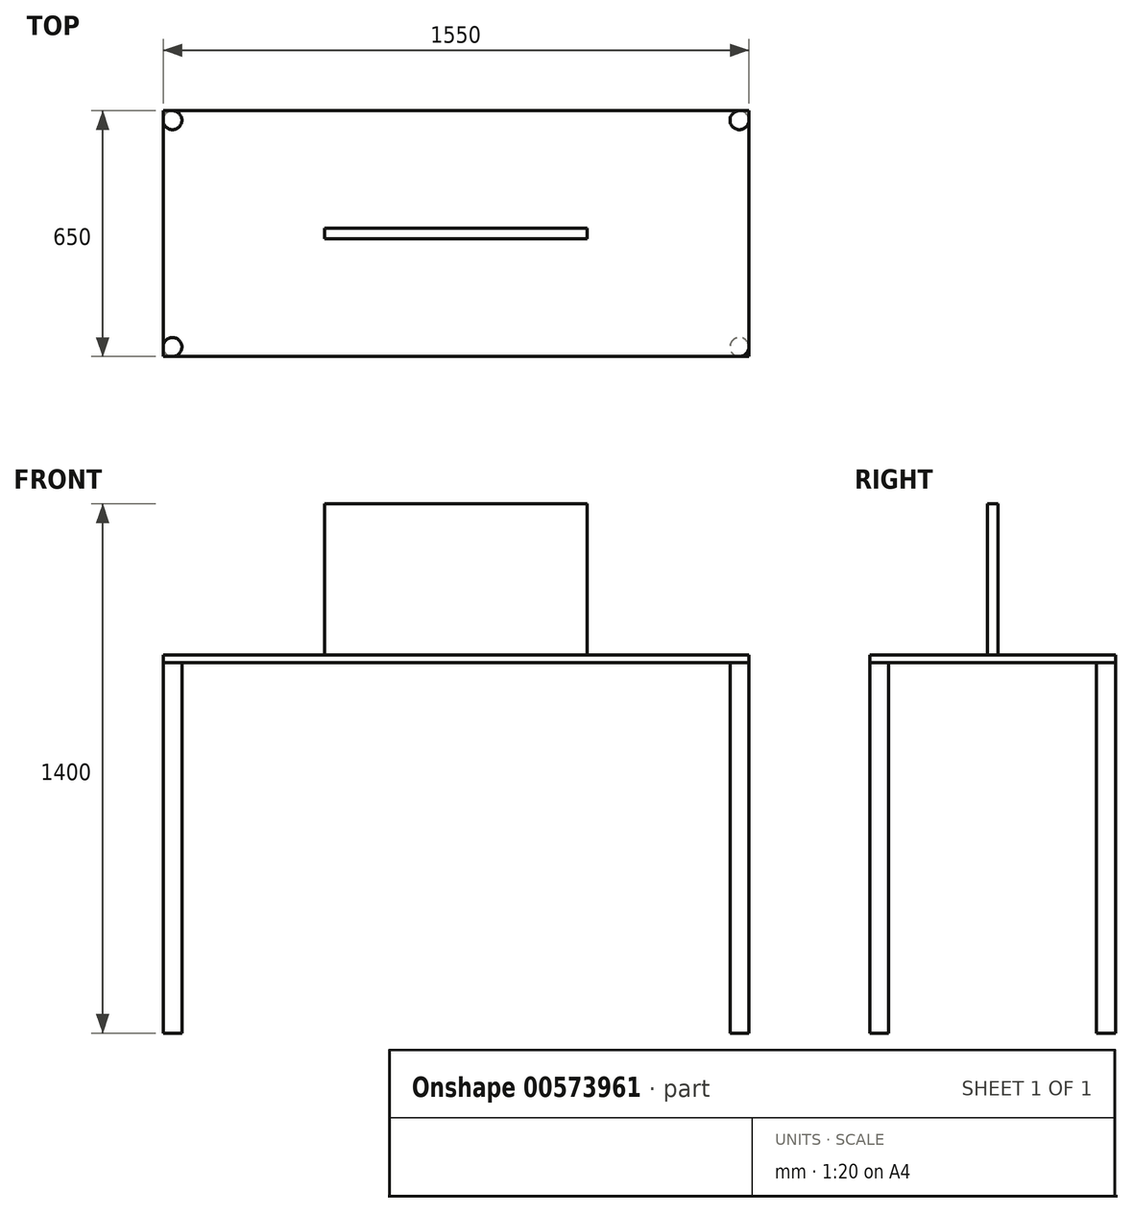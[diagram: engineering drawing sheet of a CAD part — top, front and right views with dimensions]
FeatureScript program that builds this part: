
annotation { "Feature Type Name" : "Feature", "Feature Type Description" : "" }
export const myFeature = defineFeature(function(context is Context, id is Id, definition is map)
    precondition{}
    {
        {
            var Q0;
            Q0=qCreatedBy(makeId("Top.planeOp"),FACE);
            cPlane(context, id + "F0", {"entities" : qUnion([Q0]), "cplaneType" : CPlaneType.OFFSET, "offset" : 1000 * mm, "width" : 150 * mm, "height" : 150 * mm});
        }
        {
            var Q0;
            Q0=qCreatedBy(makeId("Top.planeOp"),FACE);
            var sketch = newSketch(context, id + "F1", { "sketchPlane" : qUnion([Q0])});
            skPoint(sketch, "E0.middle", {"position": v(0, 0) * mm});
            skCircle(sketch, "E1", {"center": v(-750, 300) * mm, "radius": 25 * mm});
            skCircle(sketch, "E2", {"center": v(-750, -300) * mm, "radius": 25 * mm});
            skCircle(sketch, "E3", {"center": v(750, -300) * mm, "radius": 25 * mm});
            skCircle(sketch, "E4", {"center": v(750, 300) * mm, "radius": 25 * mm});
            skSolve(sketch);
        }
        {
            var Q0;
            Q0=qCreatedBy(id+"F0.planeOp",FACE);
            var sketch = newSketch(context, id + "F2", { "sketchPlane" : qUnion([Q0])});
            skLineSegment(sketch, "E5.bottom", {"start": v(775, 325) * mm, "end": v(-775, 325) * mm});
            skLineSegment(sketch, "E5.top", {"start": v(775, -325) * mm, "end": v(-775, -325) * mm});
            skLineSegment(sketch, "E5.left", {"start": v(775, 325) * mm, "end": v(775, -325) * mm});
            skLineSegment(sketch, "E5.right", {"start": v(-775, 325) * mm, "end": v(-775, -325) * mm});
            skSolve(sketch);
        }
        {
            var Q0;
            Q0 = qSketchRegion(id + "F1", true);
            extrude(context, id + "F3", {"entities" : qUnion([Q0]), "depth" : 980 * mm, "offsetDistance" : 25 * mm});
        }
        {
            var Q0;
            Q0 = qSketchRegion(id + "F2", true);
            extrude(context, id + "F4", {"entities" : qUnion([Q0]), "oppositeDirection" : true, "depth" : 20 * mm, "offsetDistance" : 25 * mm});
        }
        {
            var Q0;
            Q0=qCreatedBy(id+"F0.planeOp",FACE);
            var sketch = newSketch(context, id + "F5", { "sketchPlane" : qUnion([Q0])});
            skLineSegment(sketch, "E6.bottom", {"start": v(347.2, -14.1) * mm, "end": v(-347.2, -14.1) * mm});
            skLineSegment(sketch, "E6.top", {"start": v(347.2, 14.1) * mm, "end": v(-347.2, 14.1) * mm});
            skLineSegment(sketch, "E6.left", {"start": v(347.2, -14.1) * mm, "end": v(347.2, 14.1) * mm});
            skLineSegment(sketch, "E6.right", {"start": v(-347.2, -14.1) * mm, "end": v(-347.2, 14.1) * mm});
            skPoint(sketch, "E6.middle", {"position": v(0, 0) * mm});
            skSolve(sketch);
        }
        {
            var Q0;
            Q0 = qSketchRegion(id + "F5", true);
            extrude(context, id + "F6", {"entities" : qUnion([Q0]), "operationType" : NewBodyOperationType.ADD, "depth" : 400 * mm, "offsetDistance" : 25 * mm});
        }
    });
